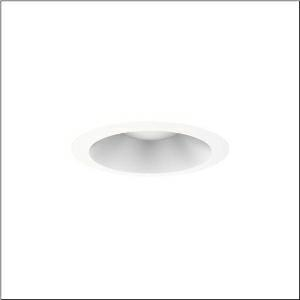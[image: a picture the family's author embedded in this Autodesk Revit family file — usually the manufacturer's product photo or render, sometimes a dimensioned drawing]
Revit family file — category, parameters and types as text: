
# Revit family: lunis_31_midi_51dn15dg42
name_source: partatom
category: Lighting Fixtures
units: mm (PartAtom-declared; Revit-internal decimal feet)

## family parameters
Cut with Voids When Loaded = No
Host = Face
Light Source = No
Part Type = Normal
Room Calculation Point = No
Round Connector Dimension = Use Diameter
Shared = No

## types (1)
- Lunis 31 midi (1 x LED, 2150 lm, 17 W, 4000K)
    Apparent Load = 17 VA
    CIE Flux Codes = 89 99 100 100 100
    Color Rendering = 80
    Color Temperature = 4000K
    Default Elevation = 1800 mm
    Description = Lunis 31,  midi, downlight, light control with reflector, light emission: direct distribution, LED rated luminous flux: 2.150lm, light colour: 840, control gear: ECG DALI, mains connection: 220..240V, AC, 50/60Hz, housing, white, protection rating (complete): IP20, insulation class (complete): insulation class II (safety insulation), certification: CE, packaging unit: 1 piece
    Height = 0 mm  [stored 0 ft]
    Lamp = 1 x LED
    Lamp Light Flux = 2150 lm
    Lamp Power = 17 W
    Lamp count = 1
    Length = 259 mm
    Luminous efficacy = 126 lm/W
    Manufacturer = Siteco
    ModVariant = No
    Model = 51DN15DG42
    Mounting Place = Ceiling
    Mounting Type = Recessed
    Number of Poles = 1
    OnlyDefault = Yes
    Power Factor = 1
    Product Name = Lunis 31 midi
    Product group = downlight | ceiling recessed
    ProductGroupID = 402
    Protection Class = Protection class II
    Protection Degree = IP 20
    RLX_Detail_Level = 1
    RlxData = <blob elided: 23717 chars, md5=b8471f68>
    Socket = socket
    Standby Power = 0 W
    System Light Flux = 2150 lm
    System Power = 17 W
    Type Comments = Product without accessories
    Type Image = l_1006711.jpg
    URL = http://relux.com
    VarID = ---
    Voltage = 0 V
    Weight = 0.00 kg
    Width = 0 mm  [stored 0 ft]

note: [stored X ft] marks values corroborated as IEEE doubles in the binary element streams (Revit-internal decimal feet)

## geometry (parser evidence)
native form markers: Blend x4, Sweep x11
no freeform markers — native parametric forms only
